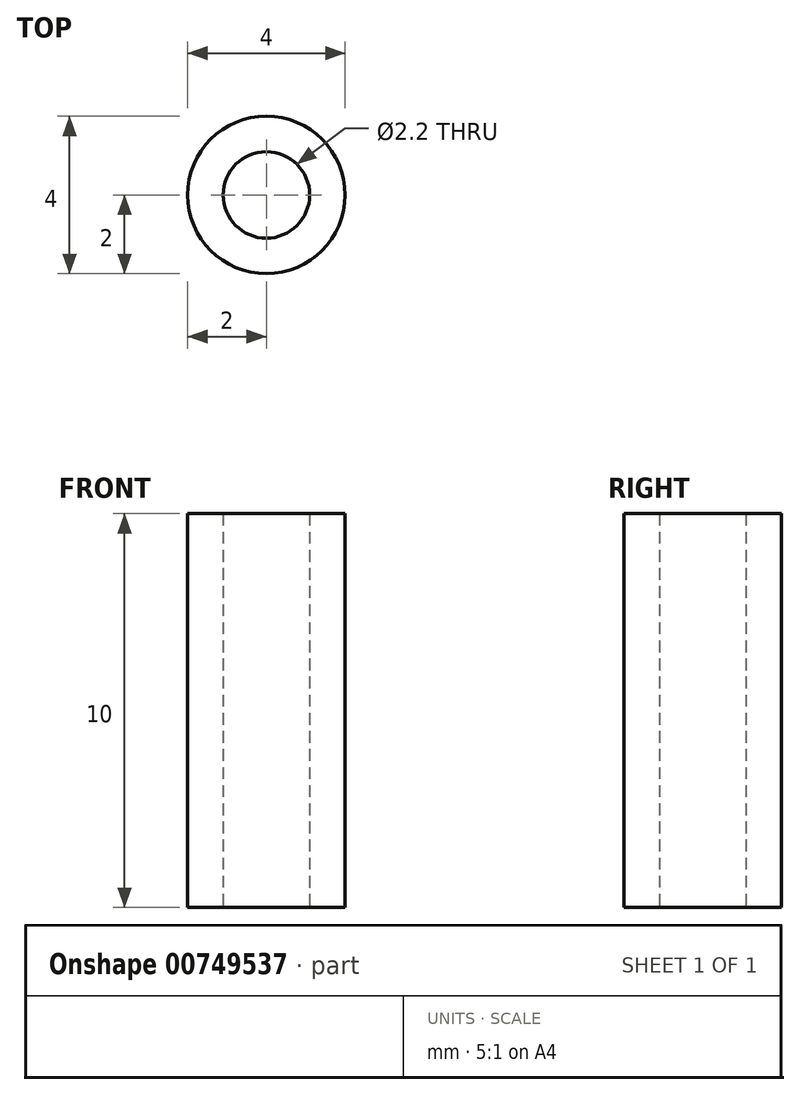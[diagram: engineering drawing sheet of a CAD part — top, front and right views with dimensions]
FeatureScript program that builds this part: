
annotation { "Feature Type Name" : "Feature", "Feature Type Description" : "" }
export const myFeature = defineFeature(function(context is Context, id is Id, definition is map)
    precondition{}
    {
        {
            var Q0;
            Q0=qCreatedBy(makeId("Top.planeOp"),FACE);
            var sketch = newSketch(context, id + "F0", { "sketchPlane" : qUnion([Q0])});
            skCircle(sketch, "E0", {"center": v(0, 0) * mm, "radius": 2 * mm});
            skCircle(sketch, "E1", {"center": v(0, 0) * mm, "radius": 1.1 * mm});
            skLineSegment(sketch, "E2", {"start": v(0, 2) * mm, "end": v(0, 5) * mm});
            skLineSegment(sketch, "E3", {"start": v(0, 5) * mm, "end": v(4, 5) * mm});
            skLineSegment(sketch, "E4", {"start": v(0, 5) * mm, "end": v(-4, 5) * mm});
            skSolve(sketch);
        }
        {
            var Q0;
            Q0=makeQuery(id+"F0.imprint","IMPRINT",FACE,{"disambiguationData":[TD([[makeQuery(id+"F0.imprint","IMPRINT",EDGE,{"derivedFrom":sQuery(id+"F0.wireOp",EDGE,"E0")}),1.0]])]});
            extrude(context, id + "F1", {"entities" : qUnion([Q0]), "depth" : 5 * mm, "offsetDistance" : 25 * mm});
        }
        {
            var Q0;
            Q0=makeQuery(id+"F1.opExtrude","CAP_FACE",FACE,{"disambiguationData":[OSD([sQuery(id+"F0.wireOp",EDGE,"E0"),sQuery(id+"F0.wireOp",EDGE,"E1")])],"isStart":true});
            extrude(context, id + "F2", {"entities" : qUnion([Q0]), "operationType" : NewBodyOperationType.ADD, "depth" : 5 * mm, "offsetDistance" : 25 * mm});
        }
    });
